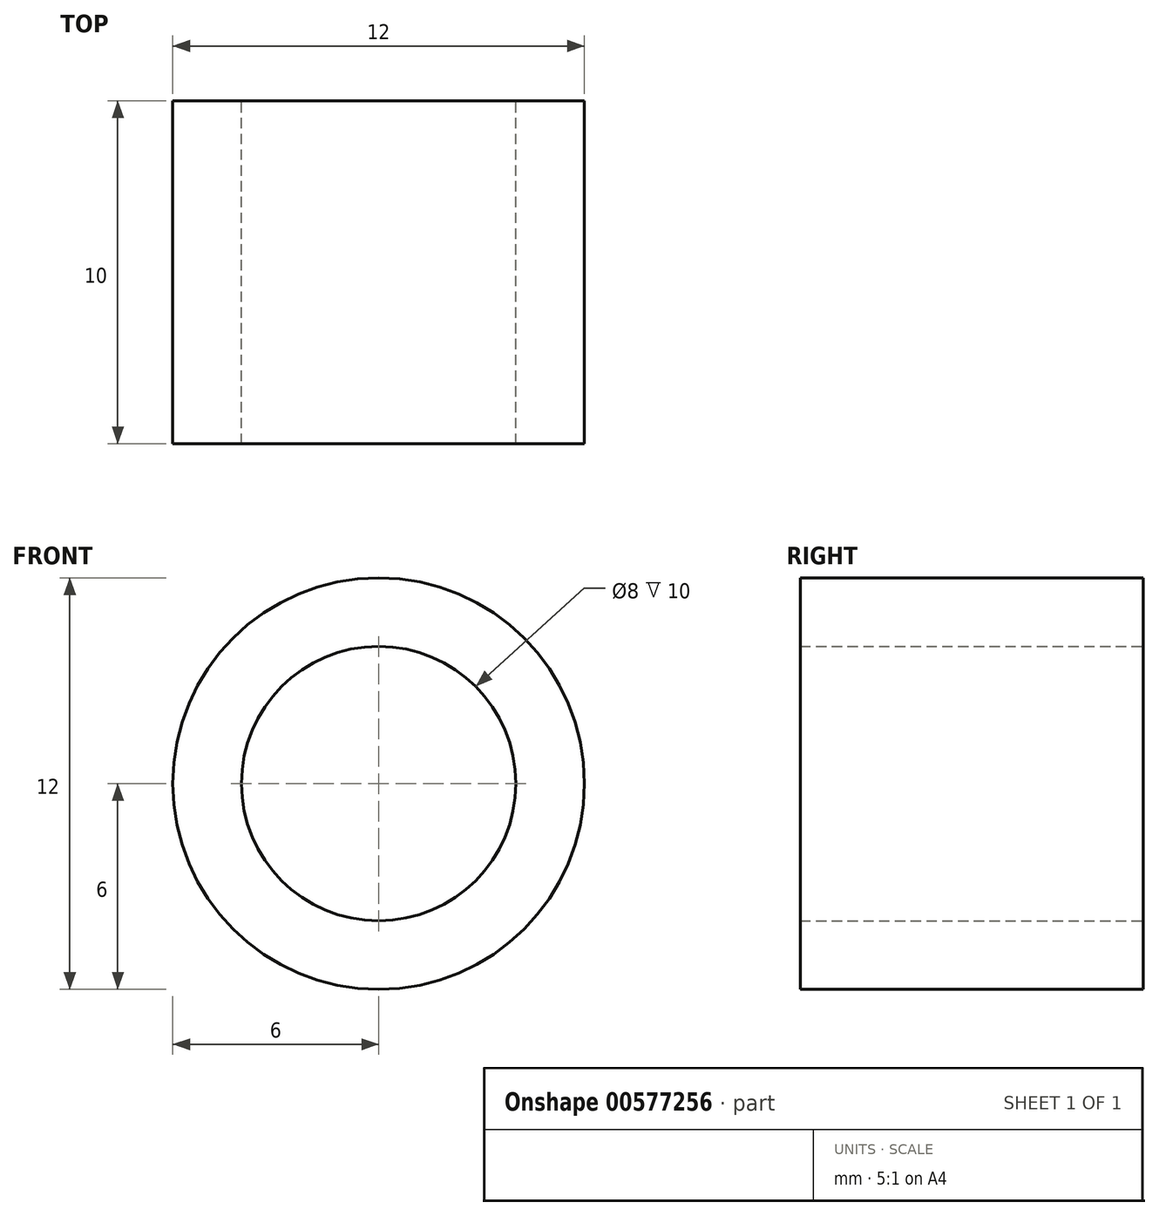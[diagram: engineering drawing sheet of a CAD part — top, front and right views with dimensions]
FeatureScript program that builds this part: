
annotation { "Feature Type Name" : "Feature", "Feature Type Description" : "" }
export const myFeature = defineFeature(function(context is Context, id is Id, definition is map)
    precondition{}
    {
        {
            var Q0;
            Q0=qCreatedBy(makeId("Front.planeOp"),FACE);
            var sketch = newSketch(context, id + "F0", { "sketchPlane" : qUnion([Q0])});
            skCircle(sketch, "E0", {"center": v(0, 0) * mm, "radius": 6 * mm});
            skCircle(sketch, "E1", {"center": v(0, 0) * mm, "radius": 4 * mm});
            skSolve(sketch);
        }
        {
            var Q0;
            Q0 = qSketchRegion(id + "F0", true);
            extrude(context, id + "F1", {"entities" : qUnion([Q0]), "endBound" : BoundingType.SYMMETRIC, "depth" : 10 * mm, "offsetDistance" : 25 * mm});
        }
    });
